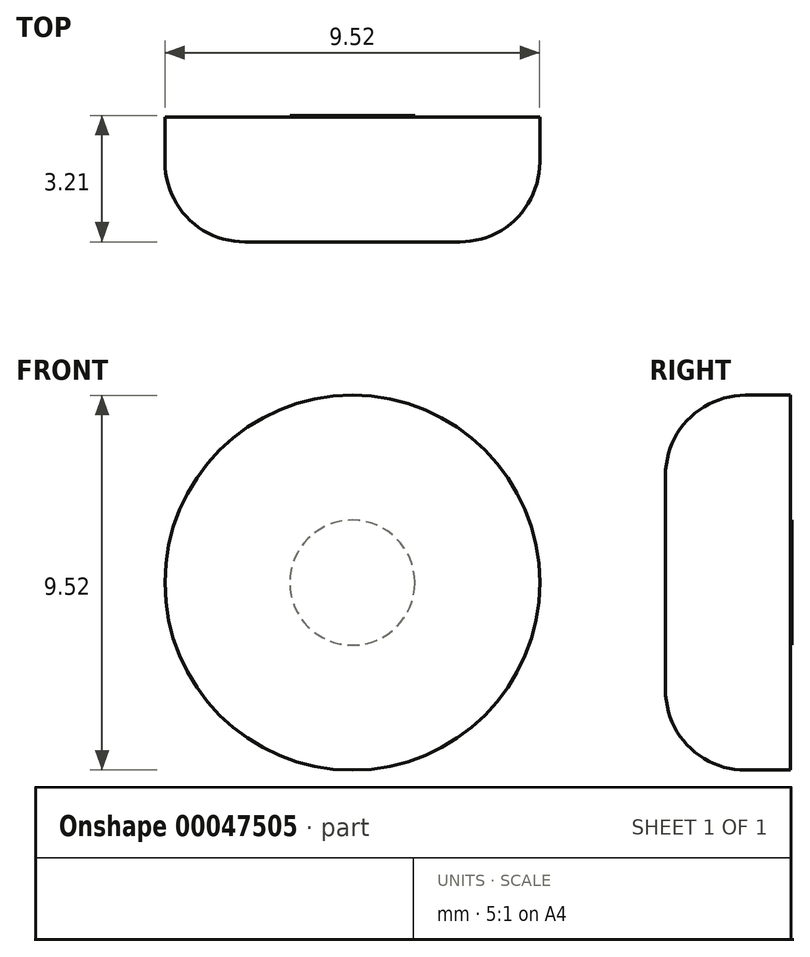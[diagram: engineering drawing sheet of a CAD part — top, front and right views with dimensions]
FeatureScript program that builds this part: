
annotation { "Feature Type Name" : "Feature", "Feature Type Description" : "" }
export const myFeature = defineFeature(function(context is Context, id is Id, definition is map)
    precondition{}
    {
        {
            var Q0;
            Q0=qCreatedBy(makeId("Front.planeOp"),FACE);
            var sketch = newSketch(context, id + "F0", { "sketchPlane" : qUnion([Q0])});
            skCircle(sketch, "E0", {"center": v(0, 0) * mm, "radius": 1.59 * mm});
            skSolve(sketch);
        }
        {
            var Q0;
            Q0=makeQuery(id+"F0.imprint","IMPRINT",FACE,{"disambiguationData":[TD([[makeQuery(id+"F0.imprint","IMPRINT",EDGE,{"derivedFrom":sQuery(id+"F0.wireOp",EDGE,"E0")}),1.0]])]});
            extrude(context, id + "F1", {"entities" : qUnion([Q0]), "endBound" : BoundingType.SYMMETRIC, "depth" : 15 / 406.4 * mm});
        }
        {
            var Q0;
            Q0=makeQuery(id+"F1.opExtrude","CAP_FACE",FACE,{"disambiguationData":[OSD([sQuery(id+"F0.wireOp",EDGE,"E0")])],"isStart":false});
            var sketch = newSketch(context, id + "F2", { "sketchPlane" : qUnion([Q0])});
            skCircle(sketch, "E1", {"center": v(0, 0) * mm, "radius": 4.76 * mm});
            skSolve(sketch);
        }
        {
            var Q0;
            Q0 = qSketchRegion(id + "F2", true);
            extrude(context, id + "F3", {"entities" : qUnion([Q0]), "operationType" : NewBodyOperationType.ADD, "depth" : 3.17 * mm});
        }
        {
            var Q0;
            Q0=makeQuery(id+"F3.opExtrude","CAP_EDGE",EDGE,{"disambiguationData":[OSD([sQuery(id+"F2.wireOp",EDGE,"E1")])],"isStart":false});
            fillet(context, id + "F4", {"entities" : qUnion([Q0]), "radius" : 2.03 * mm, "tangentPropagation" : true, "allowEdgeOverflow" : false});
        }
    });
